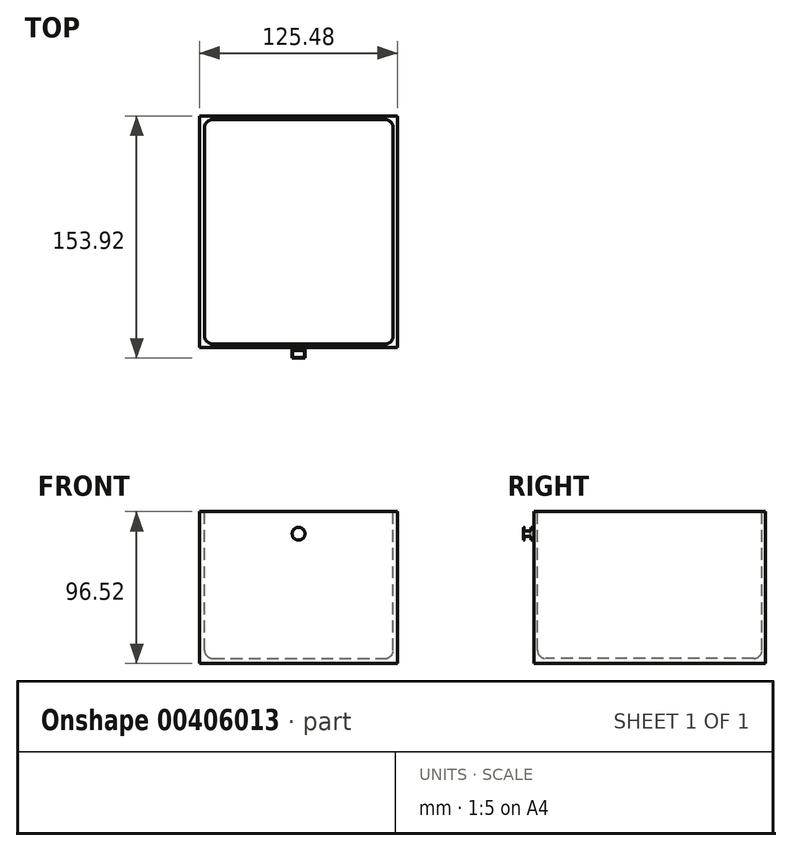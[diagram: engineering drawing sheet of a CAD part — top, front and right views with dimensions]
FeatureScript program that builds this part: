
annotation { "Feature Type Name" : "Feature", "Feature Type Description" : "" }
export const myFeature = defineFeature(function(context is Context, id is Id, definition is map)
    precondition{}
    {
        {
            var Q0;
            Q0=qCreatedBy(makeId("Front.planeOp"),FACE);
            var sketch = newSketch(context, id + "F0", { "sketchPlane" : qUnion([Q0])});
            skLineSegment(sketch, "E0.bottom", {"start": v(-62.74, 48.26) * mm, "end": v(62.74, 48.26) * mm});
            skLineSegment(sketch, "E0.top", {"start": v(-62.74, -48.26) * mm, "end": v(62.74, -48.26) * mm});
            skLineSegment(sketch, "E0.left", {"start": v(-62.74, 48.26) * mm, "end": v(-62.74, -48.26) * mm});
            skLineSegment(sketch, "E0.right", {"start": v(62.74, 48.26) * mm, "end": v(62.74, -48.26) * mm});
            skPoint(sketch, "E0.middle", {"position": v(0, 0) * mm});
            skSolve(sketch);
        }
        {
            var Q0;
            Q0 = qSketchRegion(id + "F0", true);
            extrude(context, id + "F1", {"entities" : qUnion([Q0]), "depth" : 147.07 * mm});
        }
        {
            var Q0;
            Q0=makeQuery(id+"F1.opExtrude","SWEPT_FACE",FACE,{"disambiguationData":[OSD([sQuery(id+"F0.wireOp",EDGE,"E0.bottom")])]});
            var sketch = newSketch(context, id + "F2", { "sketchPlane" : qUnion([Q0])});
            skLineSegment(sketch, "E1.bottom", {"start": v(-59.65, -2.4) * mm, "end": v(60.08, -2.4) * mm});
            skLineSegment(sketch, "E1.top", {"start": v(-59.65, -144.97) * mm, "end": v(60.08, -144.97) * mm});
            skLineSegment(sketch, "E1.left", {"start": v(-59.65, -2.4) * mm, "end": v(-59.65, -144.97) * mm});
            skLineSegment(sketch, "E1.right", {"start": v(60.08, -2.4) * mm, "end": v(60.08, -144.97) * mm});
            skSolve(sketch);
        }
        {
            var Q0;
            Q0 = qSketchRegion(id + "F2", true);
            extrude(context, id + "F3", {"entities" : qUnion([Q0]), "operationType" : NewBodyOperationType.REMOVE, "oppositeDirection" : true, "depth" : 93.22 * mm});
        }
        {
            var Q0;
            Q0=makeQuery(id+"F1.opExtrude","CAP_FACE",FACE,{"disambiguationData":[OSD([sQuery(id+"F0.wireOp",EDGE,"E0.bottom"),sQuery(id+"F0.wireOp",EDGE,"E0.top"),sQuery(id+"F0.wireOp",EDGE,"E0.left"),sQuery(id+"F0.wireOp",EDGE,"E0.right")])],"isStart":false});
            var sketch = newSketch(context, id + "F4", { "sketchPlane" : qUnion([Q0])});
            skCircle(sketch, "E2", {"center": v(0, 34.25) * mm, "radius": 4.07 * mm});
            skSolve(sketch);
        }
        {
            var Q0;
            Q0 = qSketchRegion(id + "F4", true);
            extrude(context, id + "F5", {"entities" : qUnion([Q0]), "operationType" : NewBodyOperationType.ADD, "depth" : 6.86 * mm});
        }
        {
            var Q0;
            Q0=makeQuery(id+"F3.boolean.opBoolean","COPY",FACE,{"derivedFrom":makeQuery(id+"F3.opExtrude","CAP_FACE",FACE,{"disambiguationData":[OSD([sQuery(id+"F2.wireOp",EDGE,"E1.bottom"),sQuery(id+"F2.wireOp",EDGE,"E1.top"),sQuery(id+"F2.wireOp",EDGE,"E1.left"),sQuery(id+"F2.wireOp",EDGE,"E1.right")])],"isStart":false})});
            var sketch = newSketch(context, id + "F6", { "sketchPlane" : qUnion([Q0])});
            skLineSegment(sketch, "E3.bottom", {"start": v(-3.73, -149.6) * mm, "end": v(3.73, -149.6) * mm});
            skLineSegment(sketch, "E3.top", {"start": v(-3.73, -153.41) * mm, "end": v(3.73, -153.41) * mm});
            skLineSegment(sketch, "E3.left", {"start": v(-3.73, -149.6) * mm, "end": v(-3.73, -153.41) * mm});
            skLineSegment(sketch, "E3.right", {"start": v(3.73, -149.6) * mm, "end": v(3.73, -153.41) * mm});
            skSolve(sketch);
        }
        {
            var Q0;
            Q0 = qSketchRegion(id + "F6", true);
            extrude(context, id + "F7", {"entities" : qUnion([Q0]), "operationType" : NewBodyOperationType.REMOVE, "endBound" : BoundingType.THROUGH_ALL, "depth" : 25.4 * mm});
        }
        {
            var Q0;
            Q0=makeQuery(id+"F1.opExtrude","SWEPT_FACE",FACE,{"disambiguationData":[OSD([sQuery(id+"F0.wireOp",EDGE,"E0.bottom")])]});
            var sketch = newSketch(context, id + "F8", { "sketchPlane" : qUnion([Q0])});
            skLineSegment(sketch, "E4.bottom", {"start": v(-3.7, -148.93) * mm, "end": v(3.7, -148.93) * mm});
            skLineSegment(sketch, "E4.top", {"start": v(-3.7, -152.01) * mm, "end": v(3.7, -152.01) * mm});
            skLineSegment(sketch, "E4.left", {"start": v(-3.7, -148.93) * mm, "end": v(-3.7, -152.01) * mm});
            skLineSegment(sketch, "E4.right", {"start": v(3.7, -148.93) * mm, "end": v(3.7, -152.01) * mm});
            skSolve(sketch);
        }
        {
            var Q0;
            Q0 = qSketchRegion(id + "F8", true);
            extrude(context, id + "F9", {"entities" : qUnion([Q0]), "operationType" : NewBodyOperationType.REMOVE, "endBound" : BoundingType.THROUGH_ALL, "oppositeDirection" : true, "depth" : 25.4 * mm});
        }
        {
            var Q0;
            Q0=makeQuery(id+"F3.boolean.opBoolean","COPY",EDGE,{"derivedFrom":makeQuery(id+"F3.opExtrude","SWEPT_EDGE",EDGE,{"disambiguationData":[OSD([sQuery(id+"F2.wireOp",EDGE,"E1.top"),sQuery(id+"F2.wireOp",EDGE,"E1.left")])]})});
            var Q1;
            Q1=makeQuery(id+"F3.boolean.opBoolean","COPY",EDGE,{"derivedFrom":makeQuery(id+"F3.opExtrude","CAP_EDGE",EDGE,{"disambiguationData":[OSD([sQuery(id+"F2.wireOp",EDGE,"E1.top")])],"isStart":false})});
            var Q2;
            Q2=makeQuery(id+"F3.boolean.opBoolean","COPY",EDGE,{"derivedFrom":makeQuery(id+"F3.opExtrude","CAP_EDGE",EDGE,{"disambiguationData":[OSD([sQuery(id+"F2.wireOp",EDGE,"E1.left")])],"isStart":false})});
            var Q3;
            Q3=makeQuery(id+"F3.boolean.opBoolean","COPY",EDGE,{"derivedFrom":makeQuery(id+"F3.opExtrude","CAP_EDGE",EDGE,{"disambiguationData":[OSD([sQuery(id+"F2.wireOp",EDGE,"E1.right")])],"isStart":false})});
            var Q4;
            Q4=makeQuery(id+"F3.boolean.opBoolean","COPY",EDGE,{"derivedFrom":makeQuery(id+"F3.opExtrude","SWEPT_EDGE",EDGE,{"disambiguationData":[OSD([sQuery(id+"F2.wireOp",EDGE,"E1.top"),sQuery(id+"F2.wireOp",EDGE,"E1.right")])]})});
            var Q5;
            Q5=makeQuery(id+"F3.boolean.opBoolean","COPY",EDGE,{"derivedFrom":makeQuery(id+"F3.opExtrude","CAP_EDGE",EDGE,{"disambiguationData":[OSD([sQuery(id+"F2.wireOp",EDGE,"E1.bottom")])],"isStart":false})});
            var Q6;
            Q6=makeQuery(id+"F3.boolean.opBoolean","COPY",EDGE,{"derivedFrom":makeQuery(id+"F3.opExtrude","SWEPT_EDGE",EDGE,{"disambiguationData":[OSD([sQuery(id+"F2.wireOp",EDGE,"E1.bottom"),sQuery(id+"F2.wireOp",EDGE,"E1.left")])]})});
            var Q7;
            Q7=makeQuery(id+"F3.boolean.opBoolean","COPY",EDGE,{"derivedFrom":makeQuery(id+"F3.opExtrude","SWEPT_EDGE",EDGE,{"disambiguationData":[OSD([sQuery(id+"F2.wireOp",EDGE,"E1.bottom"),sQuery(id+"F2.wireOp",EDGE,"E1.right")])]})});
            fillet(context, id + "F10", {"entities" : qUnion([Q0, Q1, Q2, Q3, Q4, Q5, Q6, Q7]), "radius" : 5.08 * mm, "tangentPropagation" : true, "allowEdgeOverflow" : false});
        }
    });
